# Revit family: BE_24429_de_DE
name_source: partatom
category: Leuchten
units: mm (PartAtom-declared; Revit-internal decimal feet)

## family parameters
Basisbauteil = Fläche
Beim Laden mit Abzugskörper schneiden = Ja
Bemaßung runder Anschluss = Durchmesser verwenden
Gemeinsam genutzt = Nein
Lichtquelle = Ja
Raumberechnungspunkt = Ja
Teiletyp = Normal

## types (4) — shared parameters
AC/DC = AC/DC
Aktualisierung = 2023-05-04T04:00:04
Befestigungsabstand = 106 mm
Befestigungsbohrung = Ø 4,3 mm
Beschreibung = Deckenaufbau-Tiefstrahler
Beschreibung_Sonderanfertigung = Hier können Sie Informationen zur Sonderanfertigung eintragen.
CE_Konformität = ja
ENEC = ja
Einbaugehäuse = Nein
Energieeffizienzklasse = LED A++ - A
Farbfilter = 16777215
Farbtemperaturverschiebung bei Dämpfen der Lampe = <Keine Auswahl>
Farbwiedergabeindex = CRI > 80
Frequenz = 0/50-60 Hz
Gewicht = 1.3 kg
Hersteller = BEGA
Höhe_Platte = -10 mm  [stored -0.0328084 ft]
Lampe = LED 8.1 W
Lastklassifizierung = Beleuchtung
Lebensdauerkriterien = L70B50 @ 25 °C = 200000 h
Logo = BEGA_Logo.png
Material_02 = BEGA_Oberfläche_Silber_matt
Material_03 = BEGA_Oberfläche_Weiss_matt
Material_06 = BEGA_Oberfläche_Edelstahl_gebürstet
Material_09 = BEGA_Glas_klar
Material_11 = BEGA_Glas_opal
Material_15 = BEGA_Leuchtmedium_matt
Material_17 = BEGA_Reflektor
Neigungswinkel = 0.00°
Netzteil_DALI_steuerbar = Nein
Netzteil_dimmbar_1_bis_10V = Nein
Produktdatenblatt = https://cdn.bega.com
Scheinlast = 0 VA
Schutzart = IP 65
Schutzklasse = I
Sonderanfertigung = Nein
Spannung = 240 V
Typenbild = 24429.png
URL = https://www.bega.com
Umgebungstemperatur = 25 °C
zero-valued in all types: D_Breite, D_Durchmesser, D_Höhe, D_Länge, Vorgabe-Ansicht

## per-type parameters (varying)
| type | Bestellnummer | Datei für fotometrisches Netz | Farbtemperatur | LED_Modulbezeichnung | Lampenlichtstrom | Leuchtenlichtstrom | M_G | M_W | Modell |
| BEGA_24429_Weiß_K4 | 24429WK4 | BE_24429K4.IES | 4000 K | LED-0800/840 | 1500 lm | 1134 lm | Nein | Ja | 24429WK4 |
| BEGA_24429_Grafit_K3 | 24429K3 | BE_24429K3.IES | 3000 K | LED-0800/830 | 1465 lm | 1108 lm | Ja | Nein | 24429K3 |
| BEGA_24429_Weiß_K3 | 24429WK3 | BE_24429K3.IES | 3000 K | LED-0800/830 | 1465 lm | 1108 lm | Nein | Ja | 24429WK3 |
| BEGA_24429_Grafit_K4 | 24429K4 | BE_24429K4.IES | 4000 K | LED-0800/840 | 1500 lm | 1134 lm | Ja | Nein | 24429K4 |

note: [stored X ft] marks values corroborated as IEEE doubles in the binary element streams (Revit-internal decimal feet)

## geometry (parser evidence)
native form markers: Blend x2
no freeform markers — native parametric forms only
